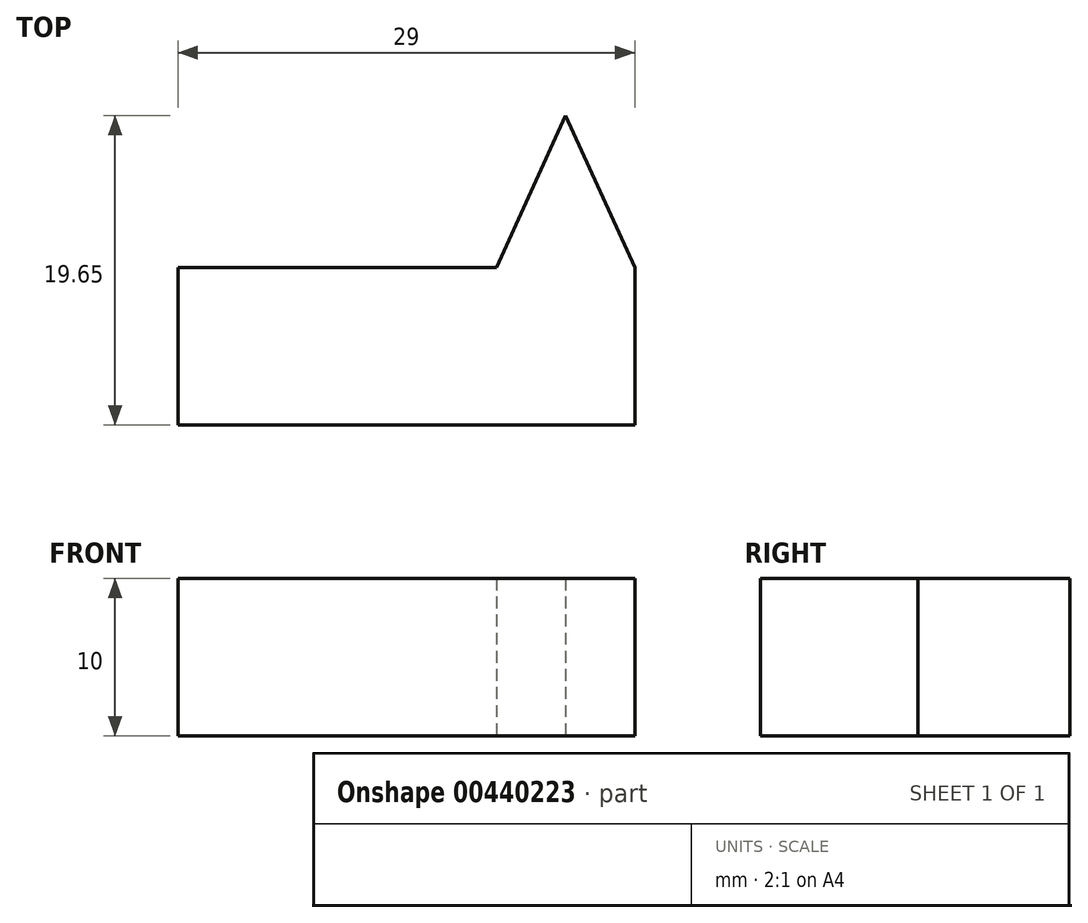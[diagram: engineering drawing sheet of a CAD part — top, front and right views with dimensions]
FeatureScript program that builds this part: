
annotation { "Feature Type Name" : "Feature", "Feature Type Description" : "" }
export const myFeature = defineFeature(function(context is Context, id is Id, definition is map)
    precondition{}
    {
        {
            var Q0;
            Q0=qCreatedBy(makeId("Top.planeOp"),FACE);
            var sketch = newSketch(context, id + "F0", { "sketchPlane" : qUnion([Q0])});
            skLineSegment(sketch, "E0.bottom", {"start": v(-14.5, 5) * mm, "end": v(14.5, 5) * mm});
            skLineSegment(sketch, "E0.top", {"start": v(-14.5, -5) * mm, "end": v(14.5, -5) * mm});
            skLineSegment(sketch, "E0.left", {"start": v(-14.5, 5) * mm, "end": v(-14.5, -5) * mm});
            skLineSegment(sketch, "E0.right", {"start": v(14.5, 5) * mm, "end": v(14.5, -5) * mm});
            skPoint(sketch, "E0.middle", {"position": v(0, 0) * mm});
            skLineSegment(sketch, "E1", {"start": v(5.73, 5) * mm, "end": v(10.12, 14.65) * mm});
            skLineSegment(sketch, "E2", {"start": v(10.12, 14.65) * mm, "end": v(14.5, 5) * mm});
            skSolve(sketch);
        }
        {
            var Q0;
            Q0 = qSketchRegion(id + "F0", true);
            extrude(context, id + "F1", {"entities" : qUnion([Q0]), "depth" : 10 * mm});
        }
    });
